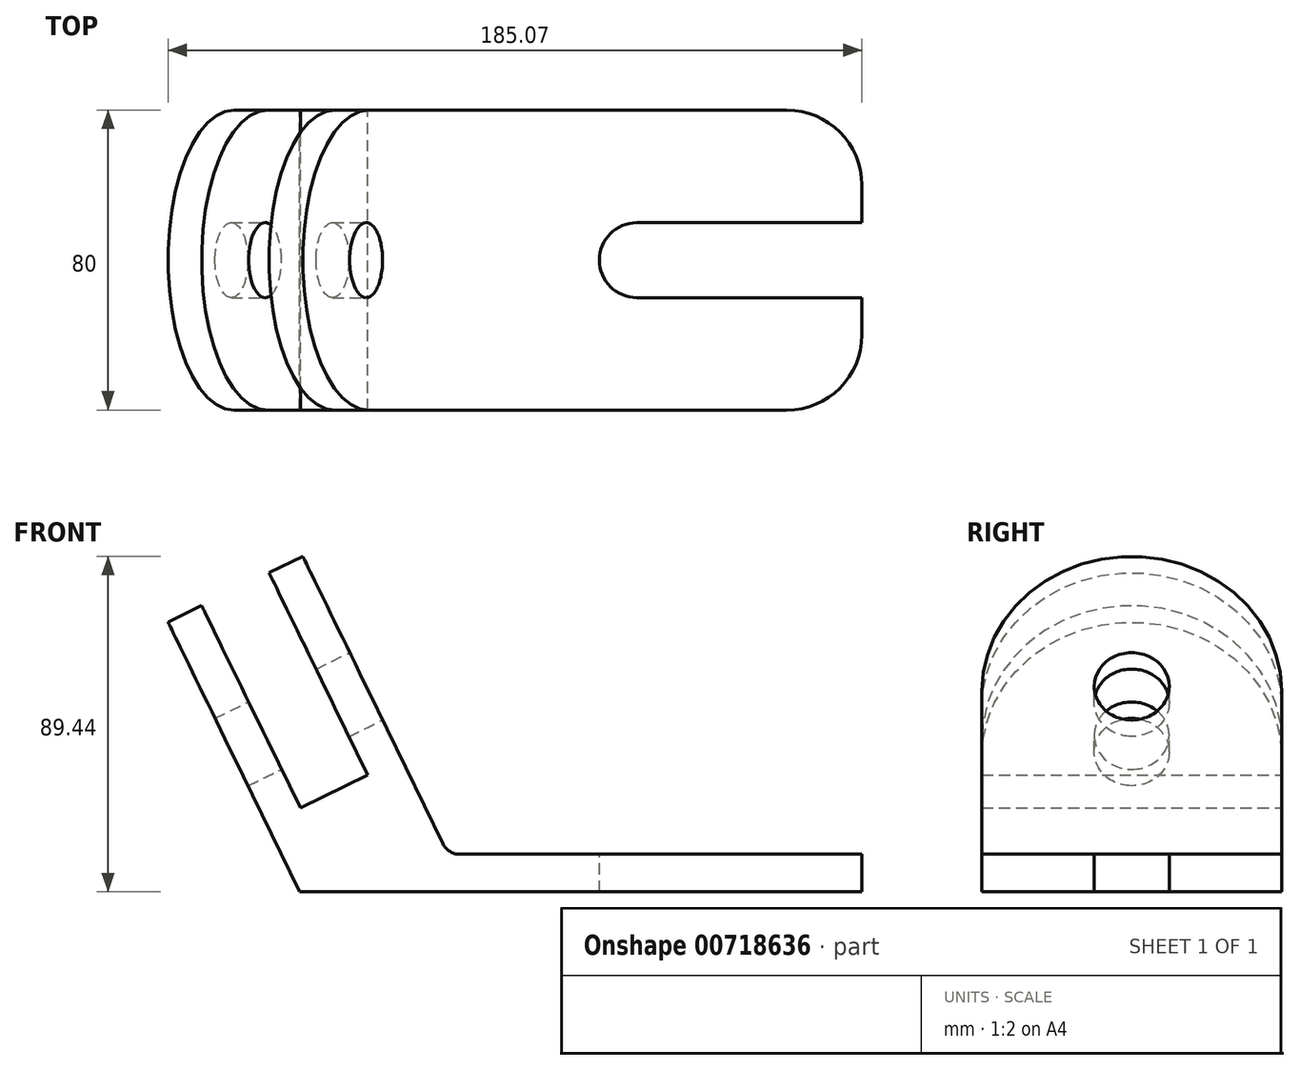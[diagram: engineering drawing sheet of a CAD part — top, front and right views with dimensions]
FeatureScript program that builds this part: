
annotation { "Feature Type Name" : "Feature", "Feature Type Description" : "" }
export const myFeature = defineFeature(function(context is Context, id is Id, definition is map)
    precondition{}
    {
        {
            var Q0;
            Q0=qCreatedBy(makeId("Front.planeOp"),FACE);
            var sketch = newSketch(context, id + "F0", { "sketchPlane" : qUnion([Q0])});
            skLineSegment(sketch, "E0", {"start": v(0, 0) * mm, "end": v(-75, 0) * mm});
            skLineSegment(sketch, "E1", {"start": v(0, 0) * mm, "end": v(75, 0) * mm});
            skLineSegment(sketch, "E2", {"start": v(-75, 0) * mm, "end": v(-110.07, 71.9) * mm});
            skLineSegment(sketch, "E3", {"start": v(75, 0) * mm, "end": v(75, 10) * mm});
            skLineSegment(sketch, "E4", {"start": v(-110.07, 71.9) * mm, "end": v(-101.08, 76.29) * mm});
            skLineSegment(sketch, "E5", {"start": v(-101.08, 76.29) * mm, "end": v(-74.78, 22.36) * mm});
            skLineSegment(sketch, "E6", {"start": v(-74.78, 22.36) * mm, "end": v(-56.8, 31.13) * mm});
            skLineSegment(sketch, "E7", {"start": v(-56.8, 31.13) * mm, "end": v(-83.1, 85.05) * mm});
            skLineSegment(sketch, "E8", {"start": v(-83.1, 85.05) * mm, "end": v(-74.12, 89.44) * mm});
            skLineSegment(sketch, "E9", {"start": v(-74.12, 89.44) * mm, "end": v(-47.82, 35.51) * mm});
            skLineSegment(sketch, "E10", {"start": v(75, 10) * mm, "end": v(-35.37, 10) * mm});
            skLineSegment(sketch, "E11", {"start": v(-47.82, 35.51) * mm, "end": v(-35.37, 10) * mm});
            skSolve(sketch);
        }
        {
            var Q0;
            Q0=makeQuery(id+"F0.imprint","IMPRINT",FACE,{"disambiguationData":[TD([[makeQuery(id+"F0.imprint","IMPRINT",EDGE,{"derivedFrom":sQuery(id+"F0.wireOp",EDGE,"E0")}),-1.0]])]});
            extrude(context, id + "F1", {"entities" : qUnion([Q0]), "depth" : 40 * mm, "offsetDistance" : 25 * mm, "hasSecondDirection" : true, "secondDirectionOppositeDirection" : true, "secondDirectionDepth" : 40 * mm});
        }
        {
            var Q0;
            Q0=makeQuery(id+"F1.opExtrude","CAP_EDGE",EDGE,{"disambiguationData":[OSD([sQuery(id+"F0.wireOp",EDGE,"E8")])],"isStart":false});
            var Q1;
            Q1=makeQuery(id+"F1.opExtrude","CAP_EDGE",EDGE,{"disambiguationData":[OSD([sQuery(id+"F0.wireOp",EDGE,"E8")])],"isStart":true});
            var Q2;
            Q2=makeQuery(id+"F1.opExtrude","CAP_EDGE",EDGE,{"disambiguationData":[OSD([sQuery(id+"F0.wireOp",EDGE,"E4")])],"isStart":false});
            var Q3;
            Q3=makeQuery(id+"F1.opExtrude","CAP_EDGE",EDGE,{"disambiguationData":[OSD([sQuery(id+"F0.wireOp",EDGE,"E4")])],"isStart":true});
            fillet(context, id + "F2", {"entities" : qUnion([Q0, Q1, Q2, Q3]), "radius" : 40 * mm, "tangentPropagation" : true, "allowEdgeOverflow" : false});
        }
        {
            var Q0;
            Q0=makeQuery(id+"F1.opExtrude","SWEPT_FACE",FACE,{"disambiguationData":[OSD([sQuery(id+"F0.wireOp",EDGE,"E10")])]});
            var sketch = newSketch(context, id + "F3", { "sketchPlane" : qUnion([Q0])});
            skArc(sketch, "E12", {"start": v(15, 10) * mm, "mid": v(5, 0) * mm, "end": v(15, -10) * mm});
            skLineSegment(sketch, "E13", {"start": v(15, 10) * mm, "end": v(75, 10) * mm});
            skLineSegment(sketch, "E14", {"start": v(15, -10) * mm, "end": v(75, -10) * mm});
            skSolve(sketch);
        }
        {
            var Q0;
            Q0=makeQuery(id+"F3.imprint","IMPRINT",FACE,{"disambiguationData":[TD([[makeQuery(id+"F3.imprint","IMPRINT",EDGE,{"derivedFrom":sQuery(id+"F3.wireOp",EDGE,"E12")}),1.0]])]});
            extrude(context, id + "F4", {"entities" : qUnion([Q0]), "operationType" : NewBodyOperationType.REMOVE, "oppositeDirection" : true, "depth" : 25 * mm, "offsetDistance" : 25 * mm});
        }
        {
            var Q0;
            Q0=makeQuery(id+"F1.opExtrude","CAP_EDGE",EDGE,{"disambiguationData":[OSD([sQuery(id+"F0.wireOp",EDGE,"E3")])],"isStart":true});
            var Q1;
            Q1=makeQuery(id+"F1.opExtrude","CAP_EDGE",EDGE,{"disambiguationData":[OSD([sQuery(id+"F0.wireOp",EDGE,"E3")])],"isStart":false});
            fillet(context, id + "F5", {"entities" : qUnion([Q0, Q1]), "radius" : 20 * mm, "tangentPropagation" : true, "allowEdgeOverflow" : false});
        }
        {
            var Q0;
            Q0=makeQuery(id+"F1.opExtrude","SWEPT_EDGE",EDGE,{"disambiguationData":[OSD([sQuery(id+"F0.wireOp",EDGE,"E10"),sQuery(id+"F0.wireOp",EDGE,"E11")])]});
            fillet(context, id + "F6", {"entities" : qUnion([Q0]), "radius" : 5 * mm, "tangentPropagation" : true, "allowEdgeOverflow" : false});
        }
        {
            var Q0;
            Q0=makeQuery(id+"F1.opExtrude","SWEPT_FACE",FACE,{"disambiguationData":[OSD([sQuery(id+"F0.wireOp",EDGE,"E9"),sQuery(id+"F0.wireOp",EDGE,"E11")])]});
            var sketch = newSketch(context, id + "F7", { "sketchPlane" : qUnion([Q0])});
            skLineSegment(sketch, "E15", {"start": v(0, 27.62) * mm, "end": v(0, 74.32) * mm});
            skCircle(sketch, "E16", {"center": v(0, 74.32) * mm, "radius": 10 * mm});
            skSolve(sketch);
        }
        {
            var Q0;
            Q0 = qSketchRegion(id + "F7", true);
            extrude(context, id + "F8", {"entities" : qUnion([Q0]), "operationType" : NewBodyOperationType.REMOVE, "oppositeDirection" : true, "depth" : 63 * mm, "offsetDistance" : 25 * mm});
        }
    });
